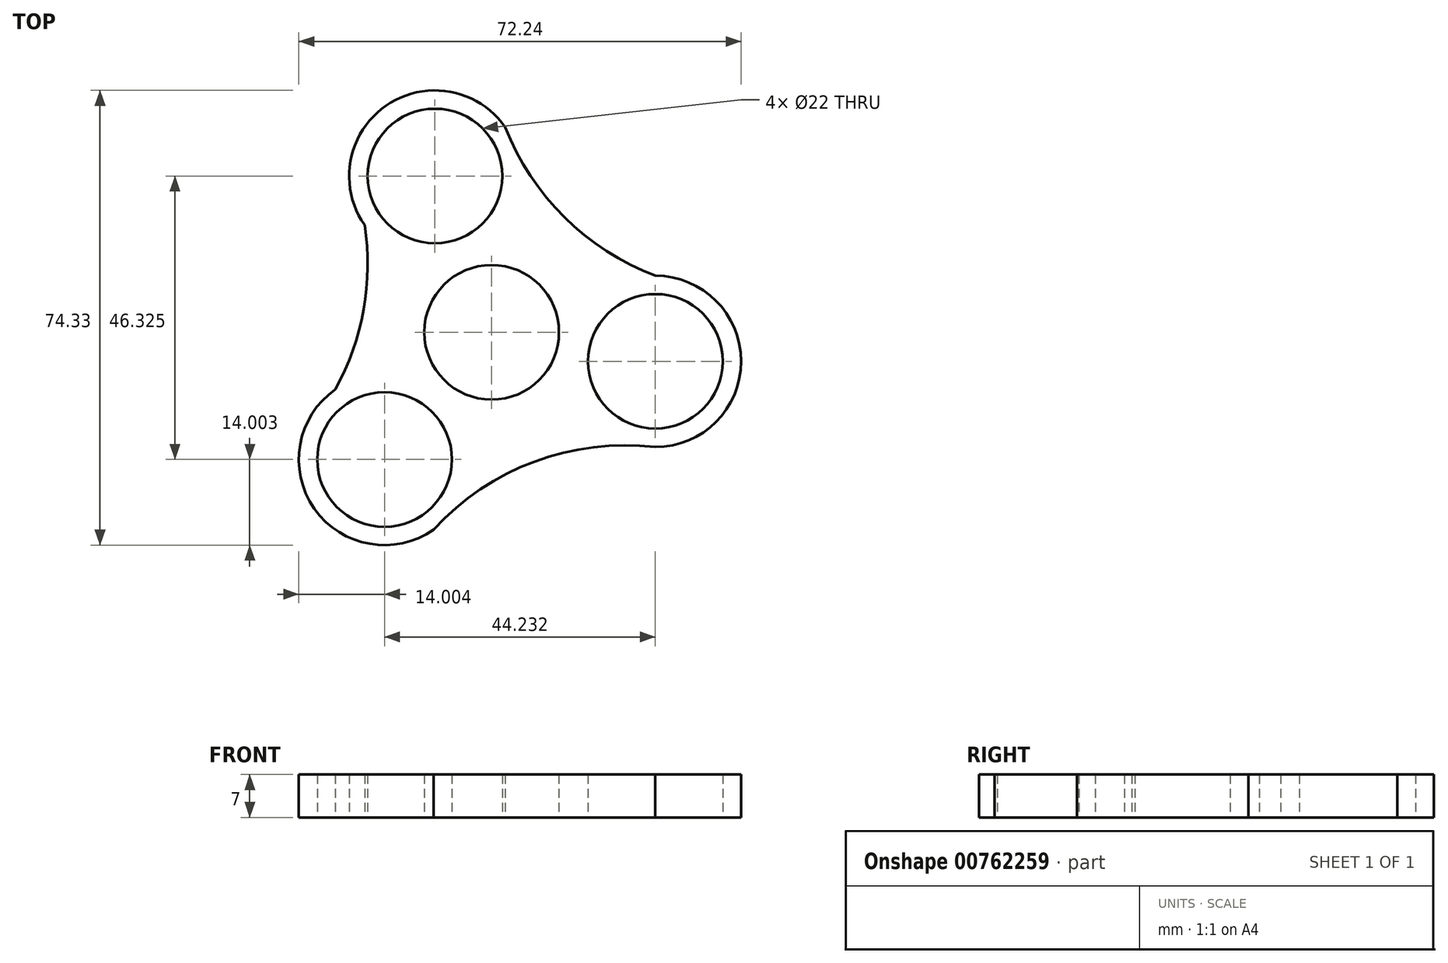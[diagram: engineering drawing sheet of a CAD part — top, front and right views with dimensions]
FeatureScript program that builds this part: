
annotation { "Feature Type Name" : "Feature", "Feature Type Description" : "" }
export const myFeature = defineFeature(function(context is Context, id is Id, definition is map)
    precondition{}
    {
        {
            var Q0;
            Q0=qCreatedBy(makeId("Top.planeOp"),FACE);
            var sketch = newSketch(context, id + "F0", { "sketchPlane" : qUnion([Q0])});
            skCircle(sketch, "E0.cCircle", {"center": v(0, 0) * mm, "radius": 27.16 * mm, "construction": true});
            skLineSegment(sketch, "E0.0", {"start": v(26.75, -4.75) * mm, "end": v(-17.49, -20.79) * mm});
            skLineSegment(sketch, "E0.1", {"start": v(-17.49, -20.79) * mm, "end": v(-9.26, 25.54) * mm});
            skLineSegment(sketch, "E0.2", {"start": v(-9.26, 25.54) * mm, "end": v(26.75, -4.75) * mm});
            skCircle(sketch, "E1", {"center": v(-9.26, 25.54) * mm, "radius": 14 * mm});
            skCircle(sketch, "E2", {"center": v(-17.49, -20.79) * mm, "radius": 11 * mm});
            skCircle(sketch, "E3", {"center": v(26.75, -4.75) * mm, "radius": 14 * mm});
            skCircle(sketch, "E4", {"center": v(26.75, -4.75) * mm, "radius": 11 * mm});
            skCircle(sketch, "E5", {"center": v(-17.49, -20.79) * mm, "radius": 14 * mm});
            skCircle(sketch, "E6", {"center": v(-9.26, 25.54) * mm, "radius": 11 * mm});
            skArc(sketch, "E7", {"start": v(-25.52, -9.32) * mm, "mid": v(-20.91, 3.71) * mm, "end": v(-20.75, 17.53) * mm});
            skLineSegment(sketch, "E8", {"start": v(-20.75, 17.53) * mm, "end": v(32.8, 54.83) * mm, "construction": true});
            skLineSegment(sketch, "E9", {"start": v(-25.52, -9.32) * mm, "end": v(0.8, -46.9) * mm, "construction": true});
            skArc(sketch, "E10", {"start": v(2.23, 33.54) * mm, "mid": v(11.9, 18.78) * mm, "end": v(26.75, 9.25) * mm});
            skLineSegment(sketch, "E11", {"start": v(26.75, 9.25) * mm, "end": v(26.75, -33.7) * mm, "construction": true});
            skArc(sketch, "E12", {"start": v(26.75, -18.75) * mm, "mid": v(7.01, -21.13) * mm, "end": v(-9.46, -32.26) * mm});
            skCircle(sketch, "E13", {"center": v(0, 0) * mm, "radius": 11 * mm});
            skSolve(sketch);
        }
        {
            var Q0;
            {var subQ5=sQuery(id+"F0.wireOp",EDGE,"E7");Q0=makeQuery(id+"F0.imprint","IMPRINT",FACE,{"disambiguationData":[TD([[makeQuery(id+"F0.imprint","IMPRINT",EDGE,{"derivedFrom":subQ5}),-1.0]])]});}
            var Q1;
            {var subQ0=sQuery(id+"F0.wireOp",EDGE,"E5");var subQ1=sQuery(id+"F0.wireOp",EDGE,"E0.0");var subQ2=makeQuery(id+"F0.imprint","INTERSECT",VERTEX,{"derivedFrom":[subQ1,subQ0]});Q1=makeQuery(id+"F0.imprint","IMPRINT",FACE,{"disambiguationData":[TD([[makeQuery(id+"F0.imprint","IMPRINT",EDGE,{"disambiguationData":[TD([[subQ2,-1.0]])],"derivedFrom":subQ1}),-1.0]])]});}
            var Q2;
            {var subQ0=sQuery(id+"F0.wireOp",EDGE,"E5");var subQ8=sQuery(id+"F0.wireOp",EDGE,"E0.0");var subQ11=makeQuery(id+"F0.imprint","INTERSECT",VERTEX,{"derivedFrom":[subQ8,subQ0]});Q2=makeQuery(id+"F0.imprint","IMPRINT",FACE,{"disambiguationData":[TD([[makeQuery(id+"F0.imprint","IMPRINT",EDGE,{"disambiguationData":[TD([[subQ11,-1.0]])],"derivedFrom":subQ8}),1.0]])]});}
            var Q3;
            {var subQ0=sQuery(id+"F0.wireOp",EDGE,"E3");var subQ1=sQuery(id+"F0.wireOp",EDGE,"E0.0");var subQ2=makeQuery(id+"F0.imprint","INTERSECT",VERTEX,{"derivedFrom":[subQ1,subQ0]});Q3=makeQuery(id+"F0.imprint","IMPRINT",FACE,{"disambiguationData":[TD([[makeQuery(id+"F0.imprint","IMPRINT",EDGE,{"disambiguationData":[TD([[subQ2,-1.0]])],"derivedFrom":subQ1}),1.0]])]});}
            var Q4;
            Q4=makeQuery(id+"F0.imprint","IMPRINT",FACE,{"disambiguationData":[TD([[makeQuery(id+"F0.imprint","IMPRINT",EDGE,{"derivedFrom":sQuery(id+"F0.wireOp",EDGE,"E13")}),-1.0]])]});
            var Q5;
            {var subQ0=sQuery(id+"F0.wireOp",EDGE,"E1");var subQ1=sQuery(id+"F0.wireOp",EDGE,"E0.1");var subQ2=makeQuery(id+"F0.imprint","INTERSECT",VERTEX,{"derivedFrom":[subQ1,subQ0]});Q5=makeQuery(id+"F0.imprint","IMPRINT",FACE,{"disambiguationData":[TD([[makeQuery(id+"F0.imprint","IMPRINT",EDGE,{"disambiguationData":[TD([[subQ2,-1.0]])],"derivedFrom":subQ1}),-1.0]])]});}
            var Q6;
            {var subQ0=sQuery(id+"F0.wireOp",EDGE,"E1");var subQ2=sQuery(id+"F0.wireOp",EDGE,"E0.1");var subQ3=makeQuery(id+"F0.imprint","INTERSECT",VERTEX,{"derivedFrom":[subQ2,subQ0]});Q6=makeQuery(id+"F0.imprint","IMPRINT",FACE,{"disambiguationData":[TD([[makeQuery(id+"F0.imprint","IMPRINT",EDGE,{"disambiguationData":[TD([[subQ3,-1.0]])],"derivedFrom":subQ2}),1.0]])]});}
            var Q7;
            {var subQ0=sQuery(id+"F0.wireOp",EDGE,"E1");var subQ1=sQuery(id+"F0.wireOp",EDGE,"E0.2");var subQ2=makeQuery(id+"F0.imprint","INTERSECT",VERTEX,{"derivedFrom":[subQ1,subQ0]});Q7=makeQuery(id+"F0.imprint","IMPRINT",FACE,{"disambiguationData":[TD([[makeQuery(id+"F0.imprint","IMPRINT",EDGE,{"disambiguationData":[TD([[subQ2,-1.0]])],"derivedFrom":subQ1}),1.0]])]});}
            var Q8;
            {var subQ0=sQuery(id+"F0.wireOp",EDGE,"E4");var subQ1=sQuery(id+"F0.wireOp",EDGE,"E0.0");var subQ2=makeQuery(id+"F0.imprint","INTERSECT",VERTEX,{"derivedFrom":[subQ1,subQ0]});Q8=makeQuery(id+"F0.imprint","IMPRINT",FACE,{"disambiguationData":[TD([[makeQuery(id+"F0.imprint","IMPRINT",EDGE,{"disambiguationData":[TD([[subQ2,-1.0]])],"derivedFrom":subQ1}),-1.0]])]});}
            var Q9;
            {var subQ3=sQuery(id+"F0.wireOp",EDGE,"E0.0");var subQ7=sQuery(id+"F0.wireOp",EDGE,"E4");var subQ10=makeQuery(id+"F0.imprint","INTERSECT",VERTEX,{"derivedFrom":[subQ3,subQ7]});Q9=makeQuery(id+"F0.imprint","IMPRINT",FACE,{"disambiguationData":[TD([[makeQuery(id+"F0.imprint","IMPRINT",EDGE,{"disambiguationData":[TD([[subQ10,-1.0]])],"derivedFrom":subQ3}),1.0]])]});}
            extrude(context, id + "F1", {"entities" : qUnion([Q0, Q1, Q2, Q3, Q4, Q5, Q6, Q7, Q8, Q9]), "depth" : 7 * mm, "offsetDistance" : 25.4 * mm});
        }
    });
